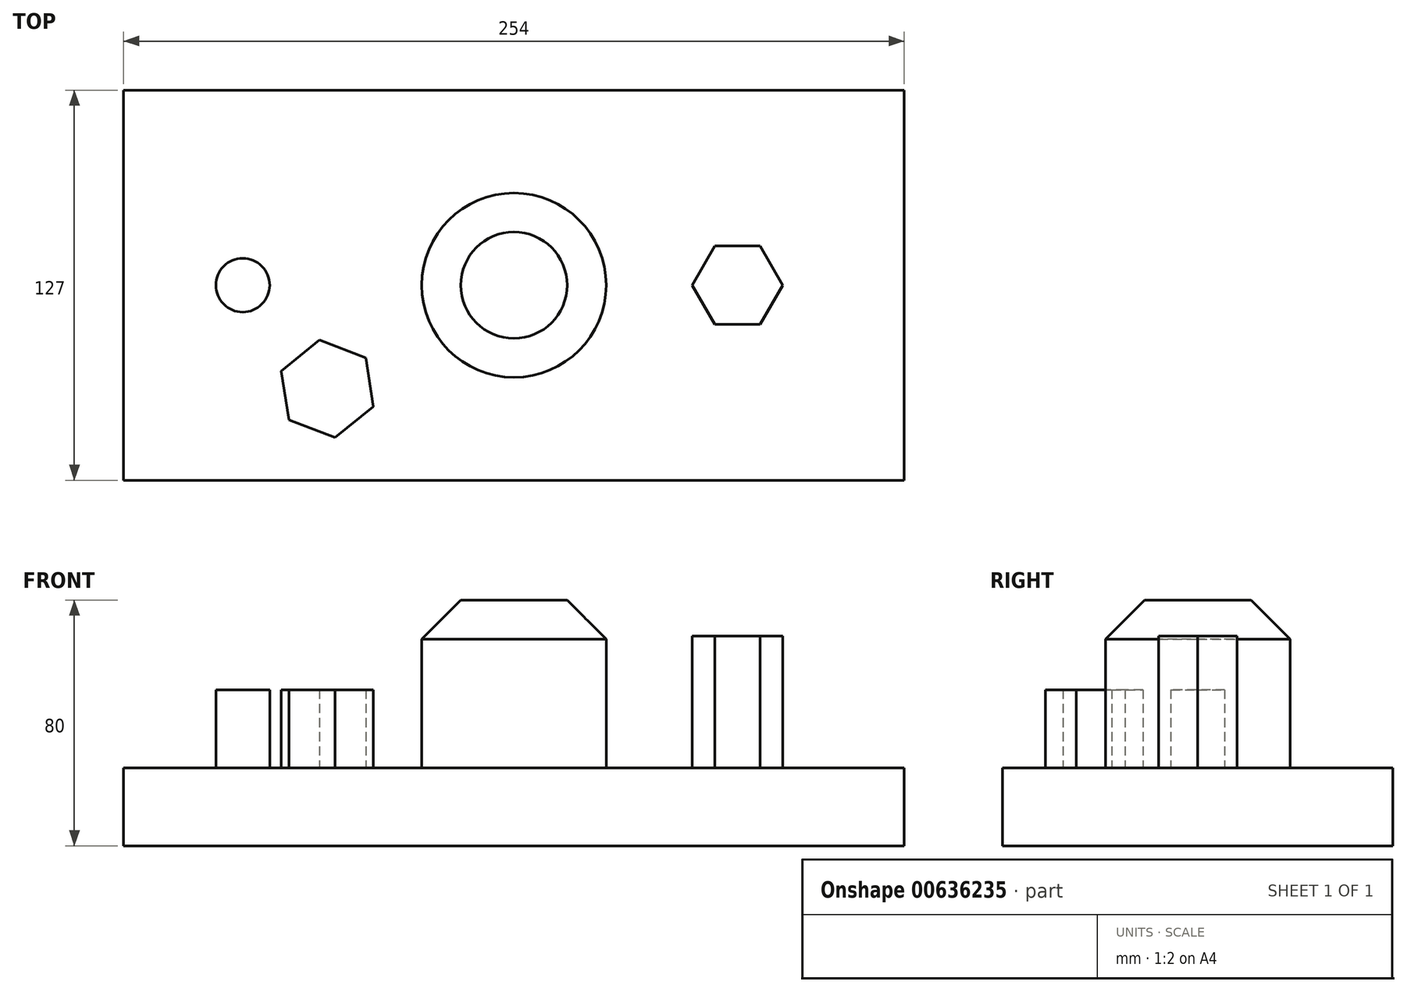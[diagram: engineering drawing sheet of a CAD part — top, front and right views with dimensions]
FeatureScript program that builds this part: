
annotation { "Feature Type Name" : "Feature", "Feature Type Description" : "" }
export const myFeature = defineFeature(function(context is Context, id is Id, definition is map)
    precondition{}
    {
        {
            var Q0;
            Q0=qCreatedBy(makeId("Top.planeOp"),FACE);
            var sketch = newSketch(context, id + "F0", { "sketchPlane" : qUnion([Q0])});
            skCircle(sketch, "E0", {"center": v(0, 0) * mm, "radius": 30 * mm});
            skSolve(sketch);
        }
        {
            var Q0;
            Q0=makeQuery(id+"F0.imprint","IMPRINT",FACE,{"disambiguationData":[TD([[makeQuery(id+"F0.imprint","IMPRINT",EDGE,{"derivedFrom":sQuery(id+"F0.wireOp",EDGE,"E0")}),1.0]])]});
            extrude(context, id + "F1", {"entities" : qUnion([Q0]), "depth" : 80 * mm, "offsetDistance" : 25 * mm});
        }
        {
            var Q0;
            Q0=qCreatedBy(makeId("Top.planeOp"),FACE);
            var sketch = newSketch(context, id + "F2", { "sketchPlane" : qUnion([Q0])});
            skLineSegment(sketch, "E1.bottom", {"start": v(-127, 63.5) * mm, "end": v(127, 63.5) * mm});
            skLineSegment(sketch, "E1.top", {"start": v(-127, -63.5) * mm, "end": v(127, -63.5) * mm});
            skLineSegment(sketch, "E1.left", {"start": v(-127, 63.5) * mm, "end": v(-127, -63.5) * mm});
            skLineSegment(sketch, "E1.right", {"start": v(127, 63.5) * mm, "end": v(127, -63.5) * mm});
            skPoint(sketch, "E1.middle", {"position": v(0, 0) * mm});
            skSolve(sketch);
        }
        {
            var Q0;
            Q0=makeQuery(id+"F2.imprint","IMPRINT",FACE,{"disambiguationData":[TD([[makeQuery(id+"F2.imprint","IMPRINT",EDGE,{"derivedFrom":sQuery(id+"F2.wireOp",EDGE,"E1.bottom")}),-1.0]])]});
            extrude(context, id + "F3", {"entities" : qUnion([Q0]), "operationType" : NewBodyOperationType.ADD, "depth" : 25.4 * mm, "offsetDistance" : 25.4 * mm});
        }
        {
            var Q0;
            Q0=makeQuery(id+"F1.opExtrude","CAP_EDGE",EDGE,{"disambiguationData":[OSD([sQuery(id+"F0.wireOp",EDGE,"E0")])],"isStart":false});
            chamfer(context, id + "F4", {"entities" : qUnion([Q0]), "width" : 12.7 * mm, "tangentPropagation" : true});
        }
        {
            var Q0;
            Q0=makeQuery(id+"F3.opExtrude","CAP_FACE",FACE,{"disambiguationData":[OSD([sQuery(id+"F2.wireOp",EDGE,"E1.bottom"),sQuery(id+"F2.wireOp",EDGE,"E1.top"),sQuery(id+"F2.wireOp",EDGE,"E1.left"),sQuery(id+"F2.wireOp",EDGE,"E1.right")])],"isStart":false});
            var sketch = newSketch(context, id + "F5", { "sketchPlane" : qUnion([Q0])});
            skCircle(sketch, "E2", {"center": v(-88.25, 0) * mm, "radius": 8.76 * mm});
            skSolve(sketch);
        }
        {
            var Q0;
            Q0=makeQuery(id+"F5.imprint","IMPRINT",FACE,{"disambiguationData":[TD([[makeQuery(id+"F5.imprint","IMPRINT",EDGE,{"derivedFrom":sQuery(id+"F5.wireOp",EDGE,"E2")}),1.0]])]});
            extrude(context, id + "F6", {"entities" : qUnion([Q0]), "operationType" : NewBodyOperationType.ADD, "depth" : 25.4 * mm, "offsetDistance" : 25.4 * mm});
        }
        {
            var Q0;
            Q0=makeQuery(id+"F3.opExtrude","CAP_FACE",FACE,{"disambiguationData":[OSD([sQuery(id+"F2.wireOp",EDGE,"E1.bottom"),sQuery(id+"F2.wireOp",EDGE,"E1.top"),sQuery(id+"F2.wireOp",EDGE,"E1.left"),sQuery(id+"F2.wireOp",EDGE,"E1.right")])],"isStart":false});
            var sketch = newSketch(context, id + "F7", { "sketchPlane" : qUnion([Q0])});
            skCircle(sketch, "E3.cCircle", {"center": v(72.75, 0) * mm, "radius": 12.75 * mm, "construction": true});
            skLineSegment(sketch, "E3.0", {"start": v(65.39, 12.75) * mm, "end": v(80.11, 12.75) * mm});
            skLineSegment(sketch, "E3.1", {"start": v(80.11, 12.75) * mm, "end": v(87.47, 0) * mm});
            skLineSegment(sketch, "E3.2", {"start": v(87.47, 0) * mm, "end": v(80.11, -12.75) * mm});
            skLineSegment(sketch, "E3.3", {"start": v(80.11, -12.75) * mm, "end": v(65.39, -12.75) * mm});
            skLineSegment(sketch, "E3.4", {"start": v(65.39, -12.75) * mm, "end": v(58.03, 0) * mm});
            skLineSegment(sketch, "E3.5", {"start": v(58.03, 0) * mm, "end": v(65.39, 12.75) * mm});
            skPoint(sketch, "E3.0.midPoint", {"position": v(72.75, 12.75) * mm});
            skSolve(sketch);
        }
        {
            var Q0;
            Q0=makeQuery(id+"F7.imprint","IMPRINT",FACE,{"disambiguationData":[TD([[makeQuery(id+"F7.imprint","IMPRINT",EDGE,{"derivedFrom":sQuery(id+"F7.wireOp",EDGE,"E3.0")}),-1.0]])]});
            extrude(context, id + "F8", {"entities" : qUnion([Q0]), "operationType" : NewBodyOperationType.ADD, "depth" : 42.93 * mm, "offsetDistance" : 25.4 * mm});
        }
        {
            var Q0;
            Q0=makeQuery(id+"F3.opExtrude","CAP_FACE",FACE,{"disambiguationData":[OSD([sQuery(id+"F2.wireOp",EDGE,"E1.bottom"),sQuery(id+"F2.wireOp",EDGE,"E1.top"),sQuery(id+"F2.wireOp",EDGE,"E1.left"),sQuery(id+"F2.wireOp",EDGE,"E1.right")])],"isStart":false});
            var sketch = newSketch(context, id + "F9", { "sketchPlane" : qUnion([Q0])});
            skCircle(sketch, "E4.cCircle", {"center": v(-60.75, -33.75) * mm, "radius": 13.93 * mm, "construction": true});
            skLineSegment(sketch, "E4.0", {"start": v(-63.26, -17.86) * mm, "end": v(-48.24, -23.64) * mm});
            skLineSegment(sketch, "E4.1", {"start": v(-48.24, -23.64) * mm, "end": v(-45.74, -39.52) * mm});
            skLineSegment(sketch, "E4.2", {"start": v(-45.74, -39.52) * mm, "end": v(-58.24, -49.64) * mm});
            skLineSegment(sketch, "E4.3", {"start": v(-58.24, -49.64) * mm, "end": v(-73.26, -43.86) * mm});
            skLineSegment(sketch, "E4.4", {"start": v(-73.26, -43.86) * mm, "end": v(-75.76, -27.98) * mm});
            skLineSegment(sketch, "E4.5", {"start": v(-75.76, -27.98) * mm, "end": v(-63.26, -17.86) * mm});
            skPoint(sketch, "E4.0.midPoint", {"position": v(-55.75, -20.75) * mm});
            skSolve(sketch);
        }
        {
            var Q0;
            Q0=makeQuery(id+"F9.imprint","IMPRINT",FACE,{"disambiguationData":[TD([[makeQuery(id+"F9.imprint","IMPRINT",EDGE,{"derivedFrom":sQuery(id+"F9.wireOp",EDGE,"E4.0")}),-1.0]])]});
            extrude(context, id + "F10", {"entities" : qUnion([Q0]), "operationType" : NewBodyOperationType.ADD, "depth" : 25.4 * mm, "offsetDistance" : 25.4 * mm});
        }
    });
